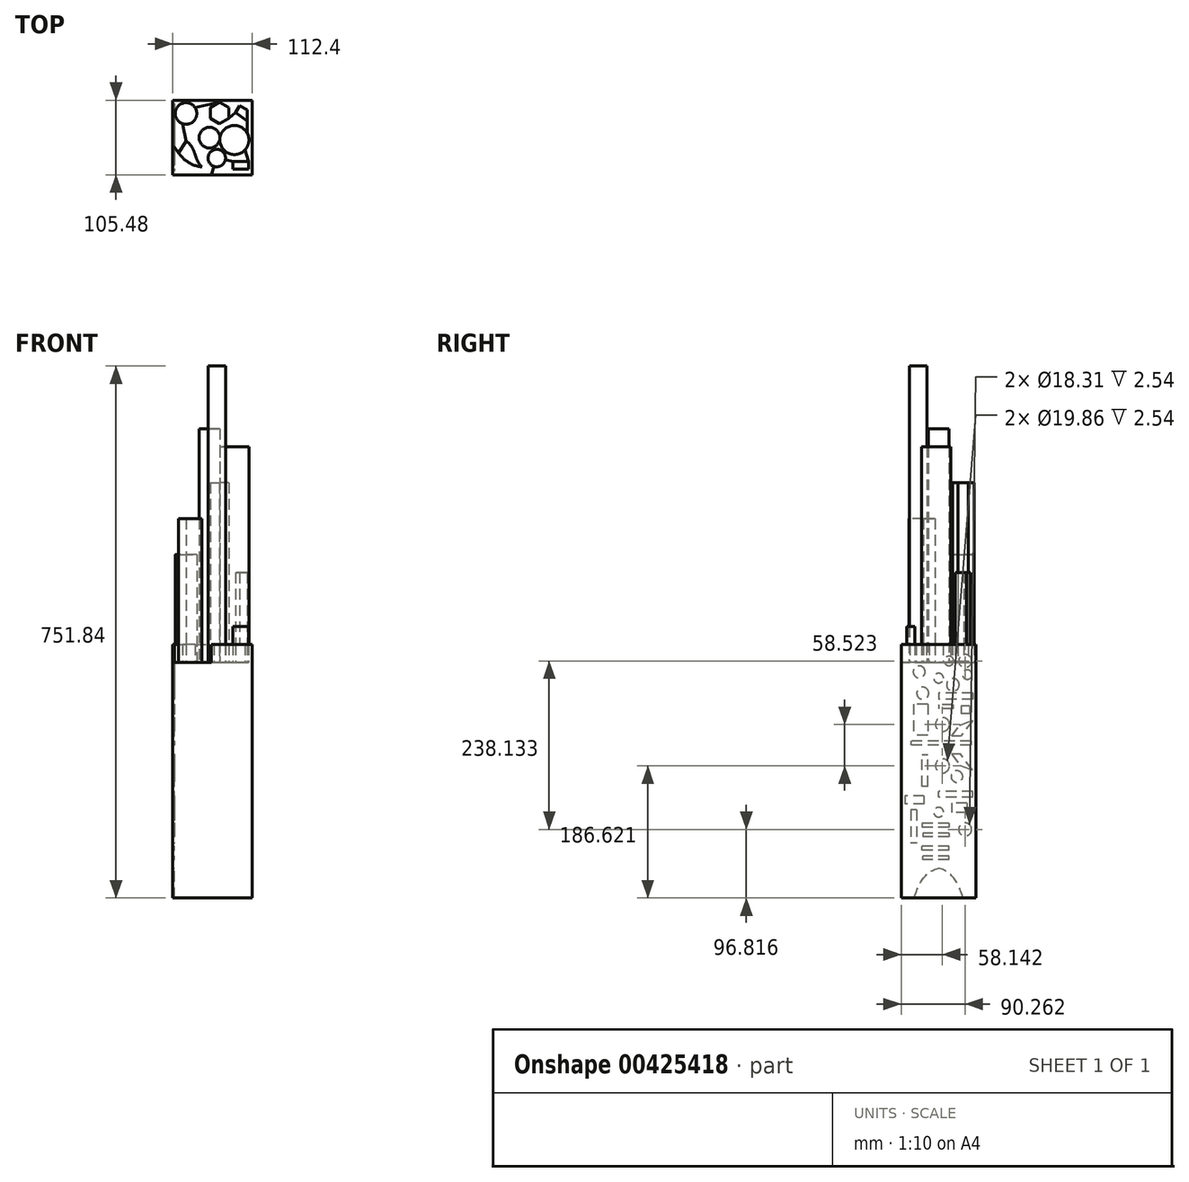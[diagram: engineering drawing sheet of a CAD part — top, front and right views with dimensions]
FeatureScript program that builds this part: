
annotation { "Feature Type Name" : "Feature", "Feature Type Description" : "" }
export const myFeature = defineFeature(function(context is Context, id is Id, definition is map)
    precondition{}
    {
        {
            var Q0;
            Q0=makeQuery(id+"FJYhYkMUMO9nOiB_0.opExtrude","CAP_FACE",FACE,{"disambiguationData":[OSD([sQuery(id+"F6aYp25Wr9Kl9S5_0.wireOp",EDGE,"b0d279b6-81f8-474c-ab90-a4ab9dabeee6"),sQuery(id+"F6aYp25Wr9Kl9S5_0.wireOp",EDGE,"8191884e-6a16-42fb-97e5-301ba8ef142f0.MirrorCS"),sQuery(id+"F6aYp25Wr9Kl9S5_0.wireOp",EDGE,"3f9235bb-c23c-4426-83ae-8f49b3e3f33d0.MirrorCS"),sQuery(id+"F6aYp25Wr9Kl9S5_0.wireOp",EDGE,"b4d13b3a-5ec0-4d23-a91b-dd21c2be0e660.MirrorCS")])],"isStart":false});
            var sketch = newSketch(context, id + "F0", { "sketchPlane" : qUnion([Q0])});
            skLineSegment(sketch, "E0.bottom", {"start": v(-5.06, 2.33) * mm, "end": v(5.32, 2.33) * mm});
            skLineSegment(sketch, "E0.top", {"start": v(-5.06, -2.33) * mm, "end": v(5.32, -2.33) * mm});
            skLineSegment(sketch, "E0.left", {"start": v(-5.06, 2.33) * mm, "end": v(-5.06, -2.33) * mm});
            skLineSegment(sketch, "E0.right", {"start": v(5.32, 2.33) * mm, "end": v(5.32, -2.33) * mm});
            skSolve(sketch);
        }
        {
            var Q0;
            Q0=makeQuery(id+"FhfQ3xYJm6Jbyuw_0.opExtrude","CAP_FACE",FACE,{"disambiguationData":[OSD([sQuery(id+"FPQG7BddbR8E6O4_0.wireOp",EDGE,"05HSuwLF-r6UH-ablM-KzuF-Vkf38imSHXgh"),sQuery(id+"FPQG7BddbR8E6O4_0.wireOp",EDGE,"jYEG8BX1-gJGz-XYVp-Evkx-MDlOE40OjlWn"),sQuery(id+"FPQG7BddbR8E6O4_0.wireOp",EDGE,"8e619b6e-52e4-4872-9997-07905d501abd0.MirrorCS"),sQuery(id+"FPQG7BddbR8E6O4_0.wireOp",EDGE,"ltnldG6F-GrSA-9rti-5cVm-JkKdsAIRv4q0")])],"isStart":false});
            var sketch = newSketch(context, id + "F1", { "sketchPlane" : qUnion([Q0])});
            skLineSegment(sketch, "E1.bottom", {"start": v(-28.66, -37.09) * mm, "end": v(-24.25, -37.09) * mm});
            skLineSegment(sketch, "E1.top", {"start": v(-28.66, -42.01) * mm, "end": v(-24.25, -42.01) * mm});
            skLineSegment(sketch, "E1.left", {"start": v(-28.66, -37.09) * mm, "end": v(-28.66, -42.01) * mm});
            skLineSegment(sketch, "E1.right", {"start": v(-24.25, -37.09) * mm, "end": v(-24.25, -42.01) * mm});
            skLineSegment(sketch, "E2.MirrorCS", {"start": v(28.66, -37.09) * mm, "end": v(24.25, -37.09) * mm});
            skLineSegment(sketch, "E3.MirrorCS", {"start": v(24.25, -37.09) * mm, "end": v(24.25, -42.01) * mm});
            skLineSegment(sketch, "E4.MirrorCS", {"start": v(28.66, -42.01) * mm, "end": v(24.25, -42.01) * mm});
            skLineSegment(sketch, "E5.MirrorCS", {"start": v(28.66, -37.09) * mm, "end": v(28.66, -42.01) * mm});
            skSolve(sketch);
        }
        {
            var Q0;
            Q0=qCreatedBy(makeId("Top.planeOp"),FACE);
            var sketch = newSketch(context, id + "F2", { "sketchPlane" : qUnion([Q0])});
            skLineSegment(sketch, "E6.bottom", {"start": v(54.93, 52.74) * mm, "end": v(-54.93, 52.74) * mm});
            skLineSegment(sketch, "E6.top", {"start": v(54.93, -52.74) * mm, "end": v(-54.93, -52.74) * mm});
            skLineSegment(sketch, "E6.left", {"start": v(54.93, 52.74) * mm, "end": v(54.93, -52.74) * mm});
            skLineSegment(sketch, "E6.right", {"start": v(-54.93, 52.74) * mm, "end": v(-54.93, -52.74) * mm});
            skPoint(sketch, "E6.middle", {"position": v(0, 0) * mm});
            skSolve(sketch);
        }
        {
            var Q0;
            Q0=makeQuery(id+"F2.imprint","IMPRINT",FACE,{"disambiguationData":[TD([[makeQuery(id+"F2.imprint","IMPRINT",EDGE,{"derivedFrom":sQuery(id+"F2.wireOp",EDGE,"E6.bottom")}),1.0]])]});
            extrude(context, id + "F3", {"entities" : qUnion([Q0]), "depth" : 332.74 * mm, "offsetDistance" : 25.4 * mm});
        }
        {
            var Q0;
            Q0=makeQuery(id+"F3.opExtrude","CAP_FACE",FACE,{"disambiguationData":[OSD([sQuery(id+"F2.wireOp",EDGE,"E6.bottom"),sQuery(id+"F2.wireOp",EDGE,"E6.top"),sQuery(id+"F2.wireOp",EDGE,"E6.left"),sQuery(id+"F2.wireOp",EDGE,"E6.right")])],"isStart":false});
            var sketch = newSketch(context, id + "F4", { "sketchPlane" : qUnion([Q0])});
            skCircle(sketch, "E7", {"center": v(-38.65, 34.12) * mm, "radius": 15.26 * mm});
            skCircle(sketch, "E8.cCircle", {"center": v(8.66, 34.64) * mm, "radius": 13.18 * mm, "construction": true});
            skLineSegment(sketch, "E8.0", {"start": v(21.84, 42.25) * mm, "end": v(21.84, 27.03) * mm});
            skLineSegment(sketch, "E8.1", {"start": v(21.84, 27.03) * mm, "end": v(8.66, 19.42) * mm});
            skLineSegment(sketch, "E8.2", {"start": v(8.66, 19.42) * mm, "end": v(-4.52, 27.03) * mm});
            skLineSegment(sketch, "E8.3", {"start": v(-4.52, 27.03) * mm, "end": v(-4.52, 42.25) * mm});
            skLineSegment(sketch, "E8.4", {"start": v(-4.52, 42.25) * mm, "end": v(8.66, 49.86) * mm});
            skLineSegment(sketch, "E8.5", {"start": v(8.66, 49.86) * mm, "end": v(21.84, 42.25) * mm});
            skPoint(sketch, "E8.0.midPoint", {"position": v(21.84, 34.64) * mm});
            skCircle(sketch, "E9", {"center": v(29.6, -3.36) * mm, "radius": 20.58 * mm});
            skCircle(sketch, "E10", {"center": v(-5.56, 0) * mm, "radius": 14.69 * mm});
            skCircle(sketch, "E11", {"center": v(4.78, -28.95) * mm, "radius": 12.32 * mm});
            skLineSegment(sketch, "E12", {"start": v(-49.12, -21.65) * mm, "end": v(-38.26, -5.1) * mm});
            skFitSpline(sketch, "E13", {"points": [v(-38.26, -5.1) * mm, v(-16.42, -41.62) * mm], "startDerivative": vector(41.1, -24.82) * mm, "endDerivative": vector(34.12, -31.8) * mm});
            skFitSpline(sketch, "E14", {"points": [v(-49.12, -21.65) * mm, v(-16.42, -41.62) * mm], "startDerivative": vector(25.6, -35.67) * mm, "endDerivative": vector(41.88, -6.2) * mm});
            skLineSegment(sketch, "E15", {"start": v(31.4, 35.42) * mm, "end": v(36.84, 45.24) * mm});
            skLineSegment(sketch, "E16", {"start": v(36.84, 45.24) * mm, "end": v(47.7, 39.24) * mm});
            skLineSegment(sketch, "E17", {"start": v(47.7, 39.24) * mm, "end": v(47.7, 23.27) * mm});
            skLineSegment(sketch, "E18", {"start": v(47.7, 23.27) * mm, "end": v(31.4, 35.42) * mm});
            skLineSegment(sketch, "E19.bottom", {"start": v(27.27, -33.6) * mm, "end": v(49.5, -33.6) * mm});
            skLineSegment(sketch, "E19.top", {"start": v(27.27, -44.72) * mm, "end": v(49.5, -44.72) * mm});
            skLineSegment(sketch, "E19.left", {"start": v(27.27, -33.6) * mm, "end": v(27.27, -44.72) * mm});
            skLineSegment(sketch, "E19.right", {"start": v(49.5, -33.6) * mm, "end": v(49.5, -44.72) * mm});
            skLineSegment(sketch, "E20", {"start": v(-16.42, -41.62) * mm, "end": v(-2.71, -52.74) * mm});
            skLineSegment(sketch, "E21", {"start": v(-49.12, -21.65) * mm, "end": v(-54.93, -13.18) * mm});
            skLineSegment(sketch, "E22", {"start": v(-38.26, -5.1) * mm, "end": v(-43.77, 19.75) * mm});
            skLineSegment(sketch, "E23", {"start": v(-25.72, 42.23) * mm, "end": v(8.66, 49.86) * mm});
            skLineSegment(sketch, "E24", {"start": v(21.84, 42.25) * mm, "end": v(21.84, 52.74) * mm});
            skLineSegment(sketch, "E25", {"start": v(21.84, 27.03) * mm, "end": v(31.4, 35.42) * mm});
            skLineSegment(sketch, "E26", {"start": v(47.7, 23.27) * mm, "end": v(47.7, 6.44) * mm});
            skLineSegment(sketch, "E27", {"start": v(47.7, 23.27) * mm, "end": v(54.93, 10.73) * mm});
            skLineSegment(sketch, "E28", {"start": v(44.77, -17.27) * mm, "end": v(49.5, -33.6) * mm});
            skLineSegment(sketch, "E29", {"start": v(27.27, -33.6) * mm, "end": v(4.78, -28.95) * mm});
            skLineSegment(sketch, "E30", {"start": v(-2.71, -52.74) * mm, "end": v(4.78, -28.95) * mm});
            skLineSegment(sketch, "E31", {"start": v(-26.76, -21.65) * mm, "end": v(-14.3, -11.8) * mm});
            skLineSegment(sketch, "E32", {"start": v(-27.92, 23.27) * mm, "end": v(-13.4, 12.43) * mm});
            skLineSegment(sketch, "E33", {"start": v(8.66, 19.42) * mm, "end": v(4.78, 12.4) * mm});
            skLineSegment(sketch, "E34", {"start": v(4.78, 12.4) * mm, "end": v(0, 13.1) * mm});
            skSolve(sketch);
        }
        {
            var Q0;
            {var subQ0=sQuery(id+"F4.wireOp",EDGE,"E7");var subQ1=makeQuery(id+"F3.opExtrude","CAP_EDGE",EDGE,{"disambiguationData":[OSD([sQuery(id+"F2.wireOp",EDGE,"E6.bottom")])],"isStart":false});var subQ2=makeQuery(id+"F4.imprint","INTERSECT",VERTEX,{"disambiguationData":[OD(0.0)],"derivedFrom":[subQ1,subQ0]});Q0=makeQuery(id+"F4.imprint","IMPRINT",FACE,{"disambiguationData":[TD([[makeQuery(id+"F4.imprint","IMPRINT",EDGE,{"disambiguationData":[TD([[subQ2,-1.0]])],"derivedFrom":subQ0}),1.0]])]});}
            var Q1;
            {var subQ0=sQuery(id+"F4.wireOp",EDGE,"E7");var subQ1=makeQuery(id+"F3.opExtrude","CAP_EDGE",EDGE,{"disambiguationData":[OSD([sQuery(id+"F2.wireOp",EDGE,"E6.right")])],"isStart":false});var subQ2=makeQuery(id+"F4.imprint","INTERSECT",VERTEX,{"disambiguationData":[OD(0.0)],"derivedFrom":[subQ1,subQ0]});Q1=makeQuery(id+"F4.imprint","IMPRINT",FACE,{"disambiguationData":[TD([[makeQuery(id+"F4.imprint","IMPRINT",EDGE,{"disambiguationData":[TD([[subQ2,-1.0]])],"derivedFrom":subQ0}),1.0]])]});}
            var Q2;
            {var subQ0=sQuery(id+"F4.wireOp",EDGE,"E7");var subQ1=makeQuery(id+"F3.opExtrude","CAP_EDGE",EDGE,{"disambiguationData":[OSD([sQuery(id+"F2.wireOp",EDGE,"E6.bottom")])],"isStart":false});var subQ2=makeQuery(id+"F4.imprint","INTERSECT",VERTEX,{"disambiguationData":[OD(0.0)],"derivedFrom":[subQ1,subQ0]});Q2=makeQuery(id+"F4.imprint","IMPRINT",FACE,{"disambiguationData":[TD([[makeQuery(id+"F4.imprint","IMPRINT",EDGE,{"disambiguationData":[TD([[subQ2,1.0]])],"derivedFrom":subQ0}),1.0]])]});}
            extrude(context, id + "F5", {"entities" : qUnion([Q0, Q1, Q2]), "operationType" : NewBodyOperationType.ADD, "depth" : 152.4 * mm, "offsetDistance" : 25.4 * mm});
        }
        {
            var Q0;
            Q0=makeQuery(id+"F4.imprint","IMPRINT",FACE,{"disambiguationData":[TD([[makeQuery(id+"F4.imprint","IMPRINT",EDGE,{"derivedFrom":sQuery(id+"F4.wireOp",EDGE,"E8.0")}),-1.0]])]});
            extrude(context, id + "F6", {"entities" : qUnion([Q0]), "operationType" : NewBodyOperationType.ADD, "depth" : 254 * mm, "offsetDistance" : 25.4 * mm});
        }
        {
            var Q0;
            {var subQ0=sQuery(id+"F4.wireOp",EDGE,"E11");var subQ1=sQuery(id+"F4.wireOp",EDGE,"E9");var subQ2=makeQuery(id+"F4.imprint","INTERSECT",VERTEX,{"disambiguationData":[OD(0.0)],"derivedFrom":[subQ1,subQ0]});Q0=makeQuery(id+"F4.imprint","IMPRINT",FACE,{"disambiguationData":[TD([[makeQuery(id+"F4.imprint","IMPRINT",EDGE,{"disambiguationData":[TD([[subQ2,1.0]])],"derivedFrom":subQ1}),1.0]])]});}
            extrude(context, id + "F7", {"entities" : qUnion([Q0]), "operationType" : NewBodyOperationType.ADD, "depth" : 25.4 * mm, "offsetDistance" : 25.4 * mm});
        }
        {
            var Q0;
            Q0=makeQuery(id+"F7.opExtrude","CAP_FACE",FACE,{"disambiguationData":[OSD([sQuery(id+"F4.wireOp",EDGE,"E9"),sQuery(id+"F4.wireOp",EDGE,"E11")])],"isStart":false});
            extrude(context, id + "F8", {"entities" : qUnion([Q0]), "operationType" : NewBodyOperationType.ADD, "depth" : 279.4 * mm, "offsetDistance" : 25.4 * mm});
        }
        {
            var Q0;
            {var subQ0=sQuery(id+"F4.wireOp",EDGE,"E11");var subQ1=sQuery(id+"F4.wireOp",EDGE,"E10");var subQ2=makeQuery(id+"F4.imprint","INTERSECT",VERTEX,{"disambiguationData":[OD(0.0)],"derivedFrom":[subQ1,subQ0]});Q0=makeQuery(id+"F4.imprint","IMPRINT",FACE,{"disambiguationData":[TD([[makeQuery(id+"F4.imprint","IMPRINT",EDGE,{"disambiguationData":[TD([[subQ2,-1.0]])],"derivedFrom":subQ1}),1.0]])]});}
            extrude(context, id + "F9", {"entities" : qUnion([Q0]), "operationType" : NewBodyOperationType.ADD, "depth" : 330.2 * mm, "offsetDistance" : 25.4 * mm});
        }
        {
            var Q0;
            Q0=makeQuery(id+"F4.imprint","IMPRINT",FACE,{"disambiguationData":[TD([[makeQuery(id+"F4.imprint","IMPRINT",EDGE,{"derivedFrom":sQuery(id+"F4.wireOp",EDGE,"E11")}),1.0]])]});
            extrude(context, id + "F10", {"entities" : qUnion([Q0]), "operationType" : NewBodyOperationType.ADD, "depth" : 419.1 * mm, "offsetDistance" : 25.4 * mm});
        }
        {
            var Q0;
            Q0=makeQuery(id+"F4.imprint","IMPRINT",FACE,{"disambiguationData":[TD([[makeQuery(id+"F4.imprint","IMPRINT",EDGE,{"derivedFrom":sQuery(id+"F4.wireOp",EDGE,"E12")}),-1.0]])]});
            extrude(context, id + "F11", {"entities" : qUnion([Q0]), "operationType" : NewBodyOperationType.ADD, "depth" : 203.2 * mm, "offsetDistance" : 25.4 * mm});
        }
        {
            var Q0;
            {var subQ0=sQuery(id+"F4.wireOp",EDGE,"E7");var subQ1=makeQuery(id+"F3.opExtrude","CAP_EDGE",EDGE,{"disambiguationData":[OSD([sQuery(id+"F2.wireOp",EDGE,"E6.right")])],"isStart":false});var subQ2=makeQuery(id+"F4.imprint","INTERSECT",VERTEX,{"disambiguationData":[OD(0.0)],"derivedFrom":[subQ1,subQ0]});Q0=makeQuery(id+"F4.imprint","IMPRINT",FACE,{"disambiguationData":[TD([[makeQuery(id+"F4.imprint","IMPRINT",EDGE,{"disambiguationData":[TD([[subQ2,-1.0]])],"derivedFrom":subQ0}),1.0]])]});}
            extrude(context, id + "F12", {"entities" : qUnion([Q0]), "operationType" : NewBodyOperationType.ADD, "depth" : 25.4 * mm, "offsetDistance" : 25.4 * mm});
        }
        {
            var Q0;
            Q0=makeQuery(id+"F4.imprint","IMPRINT",FACE,{"disambiguationData":[TD([[makeQuery(id+"F4.imprint","IMPRINT",EDGE,{"derivedFrom":sQuery(id+"F4.wireOp",EDGE,"E19.bottom")}),-1.0]])]});
            extrude(context, id + "F13", {"entities" : qUnion([Q0]), "operationType" : NewBodyOperationType.ADD, "depth" : 25.4 * mm, "offsetDistance" : 25.4 * mm});
        }
        {
            var Q0;
            Q0=makeQuery(id+"F13.opExtrude","CAP_FACE",FACE,{"disambiguationData":[OSD([sQuery(id+"F4.wireOp",EDGE,"E19.bottom"),sQuery(id+"F4.wireOp",EDGE,"E19.top"),sQuery(id+"F4.wireOp",EDGE,"E19.left"),sQuery(id+"F4.wireOp",EDGE,"E19.right")])],"isStart":false});
            extrude(context, id + "F14", {"entities" : qUnion([Q0]), "operationType" : NewBodyOperationType.ADD, "depth" : 25.4 * mm, "offsetDistance" : 25.4 * mm});
        }
        {
            var Q0;
            Q0=makeQuery(id+"F4.imprint","IMPRINT",FACE,{"disambiguationData":[TD([[makeQuery(id+"F4.imprint","IMPRINT",EDGE,{"derivedFrom":sQuery(id+"F4.wireOp",EDGE,"E15")}),-1.0]])]});
            extrude(context, id + "F15", {"entities" : qUnion([Q0]), "operationType" : NewBodyOperationType.ADD, "depth" : 127 * mm, "offsetDistance" : 25.4 * mm});
        }
        {
            var Q0;
            Q0=makeQuery(id+"F4.imprint","IMPRINT",FACE,{"disambiguationData":[TD([[makeQuery(id+"F4.imprint","IMPRINT",EDGE,{"derivedFrom":sQuery(id+"F4.wireOp",EDGE,"E8.5")}),1.0]])]});
            var Q1;
            Q1=makeQuery(id+"F4.imprint","IMPRINT",FACE,{"disambiguationData":[TD([[makeQuery(id+"F4.imprint","IMPRINT",EDGE,{"derivedFrom":sQuery(id+"F4.wireOp",EDGE,"E8.0")}),1.0]])]});
            var Q2;
            Q2=makeQuery(id+"F4.imprint","IMPRINT",FACE,{"disambiguationData":[TD([[makeQuery(id+"F4.imprint","IMPRINT",EDGE,{"derivedFrom":sQuery(id+"F4.wireOp",EDGE,"E19.top")}),-1.0]])]});
            extrude(context, id + "F16", {"entities" : qUnion([Q0, Q1, Q2]), "operationType" : NewBodyOperationType.ADD, "depth" : 25.4 * mm, "offsetDistance" : 25.4 * mm});
        }
        {
            var Q0;
            {var subQ0=sQuery(id+"F2.wireOp",EDGE,"E6.right");Q0=makeQuery(id+"F16.boolean.opBoolean","MERGE",FACE,{"derivedFrom":[makeQuery(id+"F3.opExtrude","SWEPT_FACE",FACE,{"disambiguationData":[OSD([subQ0])]}),makeQuery(id+"F16.opExtrude","SWEPT_FACE",FACE,{"disambiguationData":[OSD([subQ0])]})]});}
            var sketch = newSketch(context, id + "F17", { "sketchPlane" : qUnion([Q0])});
            skSolve(sketch);
        }
        {
            var Q0;
            {var subQ0=sQuery(id+"F2.wireOp",EDGE,"E6.right");Q0=makeQuery(id+"F17.imprint","IMPRINT",FACE,{"disambiguationData":[TD([[makeQuery(id+"F17.imprint","IMPRINT",EDGE,{"derivedFrom":makeQuery(id+"F3.opExtrude","CAP_EDGE",EDGE,{"disambiguationData":[OSD([subQ0])],"isStart":true})}),1.0]])]});}
            var sketch = newSketch(context, id + "F18", { "sketchPlane" : qUnion([Q0])});
            skCircle(sketch, "E35", {"center": v(-37.52, 334.95) * mm, "radius": 9.16 * mm});
            skCircle(sketch, "E36", {"center": v(-14.68, 334.95) * mm, "radius": 6.68 * mm});
            skCircle(sketch, "E37", {"center": v(27.53, 319.56) * mm, "radius": 8.46 * mm});
            skCircle(sketch, "E38", {"center": v(0, 310.62) * mm, "radius": 6.84 * mm});
            skCircle(sketch, "E39", {"center": v(-20.14, 301.18) * mm, "radius": 8.94 * mm});
            skCircle(sketch, "E40", {"center": v(-40.5, 315.58) * mm, "radius": 6.68 * mm});
            skCircle(sketch, "E41", {"center": v(22.4, 289.34) * mm, "radius": 8.46 * mm});
            skLineSegment(sketch, "E42.bottom", {"start": v(-48.1, 289.34) * mm, "end": v(0, 289.34) * mm});
            skLineSegment(sketch, "E42.top", {"start": v(-48.1, 280.9) * mm, "end": v(0, 280.9) * mm});
            skLineSegment(sketch, "E42.left", {"start": v(-48.1, 289.34) * mm, "end": v(-48.1, 280.9) * mm});
            skLineSegment(sketch, "E42.right", {"start": v(0, 289.34) * mm, "end": v(0, 280.9) * mm});
            skLineSegment(sketch, "E43.bottom", {"start": v(-43.64, 271.46) * mm, "end": v(-31.72, 271.46) * mm});
            skLineSegment(sketch, "E43.top", {"start": v(-43.64, 260.54) * mm, "end": v(-31.72, 260.54) * mm});
            skLineSegment(sketch, "E43.left", {"start": v(-43.64, 271.46) * mm, "end": v(-43.64, 260.54) * mm});
            skLineSegment(sketch, "E43.right", {"start": v(-31.72, 271.46) * mm, "end": v(-31.72, 260.54) * mm});
            skLineSegment(sketch, "E44.bottom", {"start": v(-20.3, 273.45) * mm, "end": v(0, 273.45) * mm});
            skLineSegment(sketch, "E44.top", {"start": v(-20.3, 267.5) * mm, "end": v(0, 267.5) * mm});
            skLineSegment(sketch, "E44.left", {"start": v(-20.3, 273.45) * mm, "end": v(-20.3, 267.5) * mm});
            skLineSegment(sketch, "E44.right", {"start": v(0, 273.45) * mm, "end": v(0, 267.5) * mm});
            skLineSegment(sketch, "E45.bottom", {"start": v(15.46, 273.95) * mm, "end": v(23.4, 273.95) * mm});
            skLineSegment(sketch, "E45.top", {"start": v(15.46, 229.75) * mm, "end": v(23.4, 229.75) * mm});
            skLineSegment(sketch, "E45.left", {"start": v(15.46, 273.95) * mm, "end": v(15.46, 229.75) * mm});
            skLineSegment(sketch, "E45.right", {"start": v(23.4, 273.95) * mm, "end": v(23.4, 229.75) * mm});
            skLineSegment(sketch, "E46.bottom", {"start": v(23.4, 273.95) * mm, "end": v(35.82, 273.95) * mm});
            skLineSegment(sketch, "E46.top", {"start": v(23.4, 229.75) * mm, "end": v(35.82, 229.75) * mm});
            skLineSegment(sketch, "E46.right", {"start": v(35.82, 273.95) * mm, "end": v(35.82, 229.75) * mm});
            skLineSegment(sketch, "E47", {"start": v(-48.1, 251.1) * mm, "end": v(-31.22, 228.76) * mm});
            skLineSegment(sketch, "E48", {"start": v(-31.22, 228.76) * mm, "end": v(-18.31, 228.76) * mm});
            skLineSegment(sketch, "E49", {"start": v(-18.31, 228.76) * mm, "end": v(-29.73, 244.15) * mm});
            skLineSegment(sketch, "E50", {"start": v(-29.73, 244.15) * mm, "end": v(-48.1, 251.1) * mm});
            skCircle(sketch, "E51", {"center": v(-5.4, 245.14) * mm, "radius": 9.93 * mm});
            skLineSegment(sketch, "E52.bottom", {"start": v(-45.8, 221.84) * mm, "end": v(39.62, 221.84) * mm});
            skLineSegment(sketch, "E52.top", {"start": v(-45.8, 215.88) * mm, "end": v(39.62, 215.88) * mm});
            skLineSegment(sketch, "E52.left", {"start": v(-45.8, 221.84) * mm, "end": v(-45.8, 215.88) * mm});
            skLineSegment(sketch, "E52.right", {"start": v(39.62, 221.84) * mm, "end": v(39.62, 215.88) * mm});
            skCircle(sketch, "E53.MirrorC", {"center": v(-5.4, 186.62) * mm, "radius": 9.93 * mm});
            skLineSegment(sketch, "E54.MirrorCS", {"start": v(-29.73, 187.61) * mm, "end": v(-48.1, 180.66) * mm});
            skLineSegment(sketch, "E55.MirrorCS", {"start": v(-18.31, 203) * mm, "end": v(-29.73, 187.61) * mm});
            skLineSegment(sketch, "E56.MirrorCS", {"start": v(-31.22, 203) * mm, "end": v(-18.31, 203) * mm});
            skLineSegment(sketch, "E57.MirrorCS", {"start": v(-48.1, 180.66) * mm, "end": v(-31.22, 203) * mm});
            skLineSegment(sketch, "E58.MirrorCS", {"start": v(15.46, 157.82) * mm, "end": v(15.46, 202.02) * mm});
            skLineSegment(sketch, "E59.MirrorCS", {"start": v(23.4, 157.82) * mm, "end": v(23.4, 202.02) * mm});
            skLineSegment(sketch, "E60.MirrorCS", {"start": v(15.46, 157.82) * mm, "end": v(23.4, 157.82) * mm});
            skLineSegment(sketch, "E61.MirrorCS", {"start": v(15.46, 202.02) * mm, "end": v(23.4, 202.02) * mm});
            skLineSegment(sketch, "E62.MirrorCS", {"start": v(-48.1, 142.42) * mm, "end": v(0, 142.42) * mm});
            skLineSegment(sketch, "E63.MirrorCS", {"start": v(-48.1, 150.87) * mm, "end": v(0, 150.87) * mm});
            skLineSegment(sketch, "E64.MirrorCS", {"start": v(0, 142.42) * mm, "end": v(0, 150.87) * mm});
            skLineSegment(sketch, "E65.MirrorCS", {"start": v(-48.1, 142.42) * mm, "end": v(-48.1, 150.87) * mm});
            skCircle(sketch, "E66.MirrorC", {"center": v(-37.52, 96.82) * mm, "radius": 9.16 * mm});
            skCircle(sketch, "E67.MirrorC", {"center": v(0, 121.15) * mm, "radius": 6.84 * mm});
            skCircle(sketch, "E68", {"center": v(-25.9, 171.54) * mm, "radius": 8.23 * mm});
            skLineSegment(sketch, "E69.bottom", {"start": v(20.75, 144.37) * mm, "end": v(47.33, 144.37) * mm});
            skLineSegment(sketch, "E69.top", {"start": v(20.75, 132.56) * mm, "end": v(47.33, 132.56) * mm});
            skLineSegment(sketch, "E69.left", {"start": v(20.75, 144.37) * mm, "end": v(20.75, 132.56) * mm});
            skLineSegment(sketch, "E69.right", {"start": v(47.33, 144.37) * mm, "end": v(47.33, 132.56) * mm});
            skLineSegment(sketch, "E70.bottom", {"start": v(-40.08, 134.33) * mm, "end": v(-18.23, 134.33) * mm});
            skLineSegment(sketch, "E70.top", {"start": v(-40.08, 120.75) * mm, "end": v(-18.23, 120.75) * mm});
            skLineSegment(sketch, "E70.left", {"start": v(-40.08, 134.33) * mm, "end": v(-40.08, 120.75) * mm});
            skLineSegment(sketch, "E70.right", {"start": v(-18.23, 134.33) * mm, "end": v(-18.23, 120.75) * mm});
            skLineSegment(sketch, "E71.bottom", {"start": v(30.8, 124.3) * mm, "end": v(39.06, 124.3) * mm});
            skLineSegment(sketch, "E71.top", {"start": v(30.8, 77.64) * mm, "end": v(39.06, 77.64) * mm});
            skLineSegment(sketch, "E71.left", {"start": v(30.8, 124.3) * mm, "end": v(30.8, 77.64) * mm});
            skLineSegment(sketch, "E71.right", {"start": v(39.06, 124.3) * mm, "end": v(39.06, 77.64) * mm});
            skLineSegment(sketch, "E72.bottom", {"start": v(-14.68, 105.4) * mm, "end": v(23.7, 105.4) * mm});
            skLineSegment(sketch, "E72.top", {"start": v(-14.68, 100.08) * mm, "end": v(23.7, 100.08) * mm});
            skLineSegment(sketch, "E72.left", {"start": v(-14.68, 105.4) * mm, "end": v(-14.68, 100.08) * mm});
            skLineSegment(sketch, "E72.right", {"start": v(23.7, 105.4) * mm, "end": v(23.7, 100.08) * mm});
            skLineSegment(sketch, "E73.bottom", {"start": v(-14.68, 91.81) * mm, "end": v(22.52, 91.81) * mm});
            skLineSegment(sketch, "E73.top", {"start": v(-14.68, 86.5) * mm, "end": v(22.52, 86.5) * mm});
            skLineSegment(sketch, "E73.left", {"start": v(-14.68, 91.81) * mm, "end": v(-14.68, 86.5) * mm});
            skLineSegment(sketch, "E73.right", {"start": v(22.52, 91.81) * mm, "end": v(22.52, 86.5) * mm});
            skLineSegment(sketch, "E74.MirrorCS", {"start": v(-14.68, 72.91) * mm, "end": v(23.7, 72.91) * mm});
            skLineSegment(sketch, "E75.MirrorCS", {"start": v(-14.68, 67.6) * mm, "end": v(23.7, 67.6) * mm});
            skLineSegment(sketch, "E76.MirrorCS", {"start": v(-14.68, 67.6) * mm, "end": v(-14.68, 72.91) * mm});
            skLineSegment(sketch, "E77.MirrorCS", {"start": v(23.7, 67.6) * mm, "end": v(23.7, 72.91) * mm});
            skLineSegment(sketch, "E78.MirrorCS", {"start": v(-14.68, 59.33) * mm, "end": v(22.52, 59.33) * mm});
            skLineSegment(sketch, "E79.MirrorCS", {"start": v(-14.68, 54.02) * mm, "end": v(22.52, 54.02) * mm});
            skLineSegment(sketch, "E80.MirrorCS", {"start": v(-14.68, 54.02) * mm, "end": v(-14.68, 59.33) * mm});
            skLineSegment(sketch, "E81.MirrorCS", {"start": v(22.52, 54.02) * mm, "end": v(22.52, 59.33) * mm});
            skFitSpline(sketch, "E82", {"points": [v(-34.58, 0) * mm, v(0, 42.04) * mm], "startDerivative": vector(23.92, 78.27) * mm, "endDerivative": vector(50.6, 14.17) * mm});
            skFitSpline(sketch, "E83.MirrorCS", {"points": [v(34.58, 0) * mm, v(0, 42.04) * mm], "startDerivative": vector(-23.92, 78.27) * mm, "endDerivative": vector(-50.6, 14.17) * mm});
            skFitSpline(sketch, "E84.0", {"points": [v(-28.5, -1.86) * mm, v(-27.55, 1.3) * mm, v(-25.58, 7.1) * mm, v(-22.49, 14.39) * mm, v(-19.22, 20.36) * mm, v(-15.78, 25.14) * mm, v(-12.12, 28.9) * mm, v(-8.12, 31.86) * mm, v(-3.62, 34.2) * mm, v(-0.16, 35.4) * mm, v(1.71, 35.92) * mm]});
            skFitSpline(sketch, "E85.0", {"points": [v(28.5, -1.86) * mm, v(27.55, 1.3) * mm, v(25.58, 7.1) * mm, v(22.49, 14.39) * mm, v(19.22, 20.36) * mm, v(15.78, 25.14) * mm, v(12.12, 28.9) * mm, v(8.12, 31.86) * mm, v(3.62, 34.2) * mm, v(0.16, 35.4) * mm, v(-1.71, 35.92) * mm]});
            skSolve(sketch);
        }
        {
            var Q0;
            Q0=makeQuery(id+"F18.imprint","IMPRINT",FACE,{"disambiguationData":[TD([[makeQuery(id+"F18.imprint","IMPRINT",EDGE,{"derivedFrom":sQuery(id+"F18.wireOp",EDGE,"E35")}),-1.0]])]});
            extrude(context, id + "F19", {"entities" : qUnion([Q0]), "operationType" : NewBodyOperationType.ADD, "depth" : 2.54 * mm, "offsetDistance" : 25.4 * mm});
        }
    });
